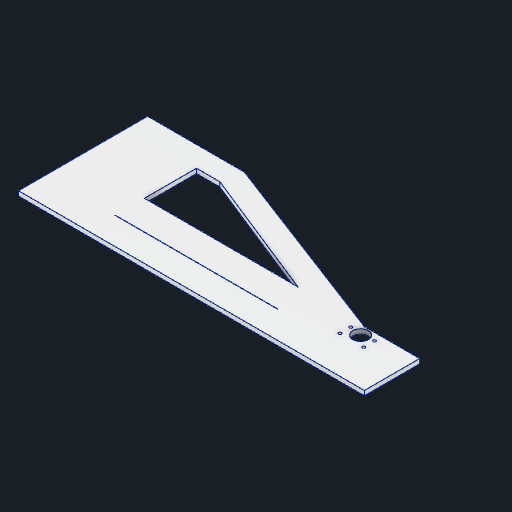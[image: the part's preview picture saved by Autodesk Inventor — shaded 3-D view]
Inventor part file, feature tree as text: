
AUTODESK INVENTOR PART (.ipt)
format: ipt  version: 2024 (Build 280153000, 153)  size: 266,752 bytes
history: native  units: mm
features: extrude x2, sketch x2, projected_geometry x1
ambient origin geometry x8: Origin, YZ Plane, XZ Plane, XY Plane, X Axis, Y Axis, Z Axis, Center Point
bodies: Body1 (feature_tree)
feature tree (5):
  extrude  "Extrusion2"  Depth=10.0mm TaperAngle=0.0deg
  extrude  "Extrusion3"  [1 undecoded]
  sketch  "Sketch3"  dims[d2=10.0mm d3=0.0mm d4=100.0mm d5=0.0mm]
  sketch  "Sketch4"
  projected_geometry  "Projected Loop1"
note: 1 required parameter value undecoded (feature->parameter linkage not recoverable at this tier; creation-order binding heuristic only, values carry confidence <= 0.55)
